# Revit family: Шкаф телекоммуникационный настенный сварной 19” 600х500
name_source: partatom
category: Обобщенные модели
units: mm (PartAtom-declared; Revit-internal decimal feet)

## family parameters
Всегда вертикально = Да
Может служить основой для арматурных стержней = Нет
На основе рабочей плоскости = Нет
Общий = Нет
При загрузке вырезать с полостями = Нет
Размер круглого соединителя = Использовать диаметр
Тип детали = Нормальный
Точка расчета площади = Нет

## types (10) — shared parameters
ADSK_URL документации изделия = https://www.ssd.ru
ADSK_URL страницы изделия = https://www.ssd.ru
ADSK_Единица измерения = шт
ADSK_Завод-изготовитель = АО СВЯЗЬСТРОЙДЕТАЛЬ
ADSK_Материал обозначение = Серый RAL 7035
ADSK_Размер_Глубина = 500 мм
ADSK_Размер_Ширина = 600 мм

## per-type parameters (varying)
| type | ADSK_Код изделия | ADSK_Масса_Текст | ADSK_Наименование | ADSK_Размер_Высота | Высота_двери | Дверь |
| ШТ-НСс 6U (600х500мм) стеклянная дверь | 130411-00739 | 17,1 | Шкаф телекоммуникационный настенный сварной 19”,6U(600x500), ШТ-НСс-6U-600-500-С дверь стекло ССД | 360 мм | 280 мм | Дверь_С |
| ШТ-НСс 6U (600х500мм) металлическая дверь | 130411-00740 | 16,7 | Шкаф телекоммуникационный настенный сварной 19”,6U(600x500), ШТ-НСс-6U-600-500-М дверь металл ССД | 360 мм | 280 мм | Дверь_М |
| ШТ-НСс 9U (600х500мм) стеклянная дверь | 130411-00745 | 20,0 | Шкаф телекоммуникационный настенный сварной 19”,9U(600x500), ШТ-НСс-9U-600-500-С дверь стекло ССД | 496 мм | 416 мм | Дверь_С |
| ШТ-НСс 9U (600х500мм) металлическая дверь | 130411-00746 | 19,5 | Шкаф телекоммуникационный настенный сварной 19”,9U(600x500), ШТ-НСс-9U-600-500-М дверь металл ССД | 496 мм | 416 мм | Дверь_М |
| ШТ-НСс 12U (600х500мм) стеклянная дверь | 130411-00751 | 22,8 | Шкаф телекоммуникационный настенный сварной 19”,12U(600x500), ШТ-НСс-12U-600-500-С дверь стекло ССД | 626 мм | 546 мм | Дверь_С |
| ШТ-НСс 12U (600х500мм) металлическая дверь | 130411-00752 | 22,0 | Шкаф телекоммуникационный настенный сварной 19”,12U(600x500), ШТ-НСс-12U-600-500-М дверь металл ССД | 626 мм | 546 мм | Дверь_М |
| ШТ-НСс 15U (600х500мм) стеклянная дверь | 130411-00757 | 25,5 | Шкаф телекоммуникационный настенный сварной 19”,15U(600x500), ШТ-НСс-15U-600-500-С дверь стекло ССД | 760 мм | 680 мм | Дверь_С |
| ШТ-НСс 15U (600х500мм) металлическая дверь | 130411-00758 | 24,6 | Шкаф телекоммуникационный настенный сварной 19”,15U(600x500), ШТ-НСс-15U-600-500-М дверь металл ССД | 760 мм | 680 мм | Дверь_М |
| ШТ-НСс 18U (600х500мм) стеклянная дверь | 130411-00763 | 28,3 | Шкаф телекоммуникационный настенный сварной 19”,18U(600x500), ШТ-НСс-18U-600-500-С дверь стекло ССД | 893 мм | 813 мм | Дверь_С |
| ШТ-НСс 18U (600х500мм) металлическая дверь | 130411-00764 | 25,4 | Шкаф телекоммуникационный настенный сварной 19”,18U(600x500), ШТ-НСс-18U-600-500-М дверь металл ССД | 893 мм | 813 мм | Дверь_М |

note: column(s) folded — value = type name in every type: ADSK_Обозначение
